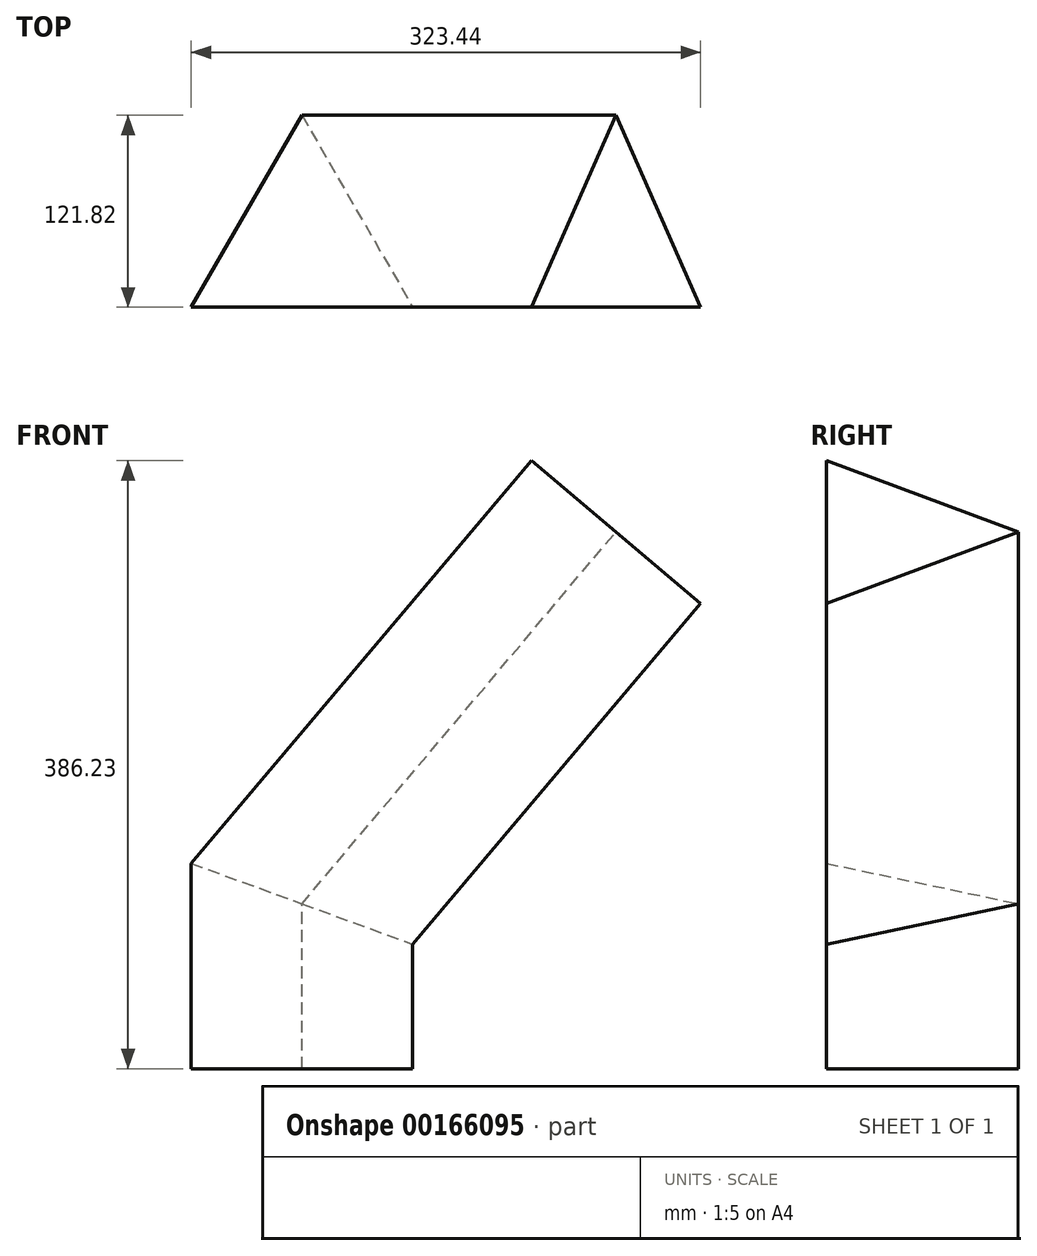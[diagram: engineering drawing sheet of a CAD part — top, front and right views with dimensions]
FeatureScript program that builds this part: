
annotation { "Feature Type Name" : "Feature", "Feature Type Description" : "" }
export const myFeature = defineFeature(function(context is Context, id is Id, definition is map)
    precondition{}
    {
        {
            var Q0;
            Q0=qCreatedBy(makeId("Top.planeOp"),FACE);
            var sketch = newSketch(context, id + "F0", { "sketchPlane" : qUnion([Q0])});
            skCircle(sketch, "E0.cCircle", {"center": v(0, 0) * mm, "radius": 40.6 * mm, "construction": true});
            skLineSegment(sketch, "E0.0", {"start": v(70.33, -40.6) * mm, "end": v(-70.33, -40.6) * mm});
            skLineSegment(sketch, "E0.1", {"start": v(-70.33, -40.6) * mm, "end": v(0, 81.21) * mm});
            skLineSegment(sketch, "E0.2", {"start": v(0, 81.21) * mm, "end": v(70.33, -40.6) * mm});
            skPoint(sketch, "E0.0.midPoint", {"position": v(0, -40.6) * mm});
            skSolve(sketch);
        }
        {
            var Q0;
            Q0=qCreatedBy(makeId("Front.planeOp"),FACE);
            var sketch = newSketch(context, id + "F1", { "sketchPlane" : qUnion([Q0])});
            skLineSegment(sketch, "E1", {"start": v(0, 0) * mm, "end": v(0, 104.73) * mm});
            skLineSegment(sketch, "E2", {"start": v(0, 104.73) * mm, "end": v(199.37, 340.86) * mm});
            skSolve(sketch);
        }
        {
            var Q0;
            Q0 = qSketchRegion(id + "F0", true);
            var Q1;
            Q1=sQuery(id+"F1.wireOp",EDGE,"E1");
            var Q2;
            Q2=sQuery(id+"F1.wireOp",EDGE,"E2");
            sweep(context, id + "F2", {"profiles" : qUnion([Q0]), "path" : qUnion([Q1, Q2])});
        }
    });
